# Revit family: Indirect-Water-Heater_AO_Smith-ITS-400_B_B
name_source: partatom
category: Mechanical Equipment
revit_build: Autodesk Revit 2016 (Build: 20170117_1200(x64)
units: mm (PartAtom-declared; Revit-internal decimal feet)

## family parameters
Always vertical = Yes
Cut with Voids When Loaded = No
OmniClass Number = 23.75.00.00
OmniClass Title = Climate Control (HVAC)
Part Type = Normal
Room Calculation Point = No
Round Connector Dimension = Use Radius
Shared = No
Work Plane-Based = No

## types (1)
- Indirect-Water-Heater_AO_Smith-ITS-400_B_B
    1er Entretien (check-up) = 3 mois après l'installation
    2ème Entretien (Entretien Général) = 12 mois après l'installation
    Assembly Code = D3010
    BIM Content Developer = CAD & Company
    BIM Content Developer URL = http://www.cadcompany.nl
    Capacité - Cuve = 382 m³
    Capacité - Échangeur Inférieur = 9.9 m³
    Capacité - Échangeur Supérieur = 6.9 m³
    Charge Maximale au Sol = 527.00 kg
    Description = Cuve Indirects Fournis d’un Échangeur
    Destination / Pays = Belgique
    Diamètre (avec Isolation) = 740 mm  [stored 2.42782 ft]
    Diamètre (sans Isolation) = 600 mm  [stored 1.9685 ft]
    Débit de vidage en Continu à ΔT = 28°C = 2734
    Débit de vidage en Continu à ΔT = 44°C = 0
    Débit de vidage en Continu à ΔT = 50°C = 1531
    Débit de vidage en Continu à ΔT = 55°C = 0
    Débit de vidage en Continu à ΔT = 70°C = 1093
    Débit de vidage à ΔT = 28°C après 120 min. = 6095.0 L
    Débit de vidage à ΔT = 28°C après 30 min. = 1994.0 L
    Débit de vidage à ΔT = 28°C après 60 min. = 3361.0 L
    Débit de vidage à ΔT = 28°C après 90 min. = 4728.0 L
    Débit de vidage à ΔT = 44°C après 120 min. = 0.0 L
    Débit de vidage à ΔT = 44°C après 30 min. = 0.0 L
    Débit de vidage à ΔT = 44°C après 60 min. = 0.0 L
    Débit de vidage à ΔT = 44°C après 90 min. = 0.0 L
    Débit de vidage à ΔT = 50°C après 120 min. = 3413.0 L
    Débit de vidage à ΔT = 50°C après 30 min. = 1117.0 L
    Débit de vidage à ΔT = 50°C après 60 min. = 1882.0 L
    Débit de vidage à ΔT = 50°C après 90 min. = 2648.0 L
    Débit de vidage à ΔT = 55°C après 120 min. = 0.0 L
    Débit de vidage à ΔT = 55°C après 30 min. = 0.0 L
    Débit de vidage à ΔT = 55°C après 60 min. = 0.0 L
    Débit de vidage à ΔT = 55°C après 90 min. = 0.0 L
    Débit de vidage à ΔT = 70°C après 120 min. = 2438.0 L
    Débit de vidage à ΔT = 70°C après 30 min. = 798.0 L
    Débit de vidage à ΔT = 70°C après 60 min. = 1344.0 L
    Débit de vidage à ΔT = 70°C après 90 min. = 1891.0 L
    Débit à 80ºC/60ºC - Échangeur Inférieur = 2236
    Débit à 80ºC/60ºC - Échangeur Supérieur = 1591
    Epaisseur d'Isolation = 70 mm  [stored 0.229659 ft]
    Fabricant No. = E 7110
    Garantie Pièces = 12 mois
    Garantie sur la Cuve = 36 mois
    Guide de Produit = https://www.aosmithinternational.com
    Hauteur (avec Isolation) = 1710 mm  [stored 5.61024 ft]
    Hauteur (sans Isolation) = 1655 mm  [stored 5.42979 ft]
    Hauteur d'Emballage = 1850 mm  [stored 6.06955 ft]
    Hauteur de l'Alimentation en eau Froide = 70 mm  [stored 0.229659 ft]
    Hauteur de la Sortie d'eau Chaude = 1655 mm  [stored 5.42979 ft]
    Largeur d'Emballage = 780 mm  [stored 2.55906 ft]
    Manufacturer = A.O. Smith Water Products Company b.v.
    Max. Température de l'eau - Réservoir = 95 °C
    Model = ITS 400 B B
    Niveau du Son = 0
    Nombre de modèle du produit (EAN) = 8717449181536
    Perte de Pression à 80ºC/60ºC - Échangeur Inférieur = 7800.0 Pa
    Perte de Pression à 80ºC/60ºC - Échangeur Supérieur = 3000.0 Pa
    Pertes en Veille = 0 W
    Pertes en Veille - tous les jours (24h) = 0
    Poids de Transport = 156.00 kg
    Poids à vide = 145.00 kg
    Pression de Service Maximale - Réservoir = 1000000.0 Pa
    Pression de Service Maximale - Échangeur Inférieur = 1600000.0 Pa
    Pression de Service Maximale - Échangeur Supérieur = 1600000.0 Pa
    Production Nominale - Échangeur Inférieur = 52000 W
    Production Nominale - Échangeur Supérieur = 37000 W
    Profondeur d'Emballage = 780 mm  [stored 2.55906 ft]
    Raccord d'Alimentation en Eau Froide = 2"
    Raccord de Sortie d'Eau Chaude = 2"
    Raccord de la Soupape de Vidange = 1"
    Spécifications du Produit = https://www.aosmithinternational.com
    Surface d'Échange de Chaleur - Échangeur Inférieur = 1.64 m²
    Surface d'Échange de Chaleur - Échangeur Supérieur = 1.15 m²
    Temps de réchauffement à ΔT = 28°C = 8
    Temps de réchauffement à ΔT = 44°C = 0
    Temps de réchauffement à ΔT = 50°C = 15
    Temps de réchauffement à ΔT = 55°C = 0
    Temps de réchauffement à ΔT = 70°C = 21
    Température Maximale - Échangeur Inférieur = 110 °C
    Température Maximale - Échangeur Supérieur = 110 °C
    Type d'Emballage = Plastique et Bois
    URL = https://www.aosmithinternational.com
    Workspace Diameter = 1740 mm
    Workspace Height = 2710 mm  [stored 8.89108 ft]
    espace de travail = 860 mm
    l'Intervalle d'Entretien = 12 mois

note: [stored X ft] marks values corroborated as IEEE doubles in the binary element streams (Revit-internal decimal feet)

## geometry (parser evidence)
native form markers: Blend x2, Sweep x21
no freeform markers — native parametric forms only
